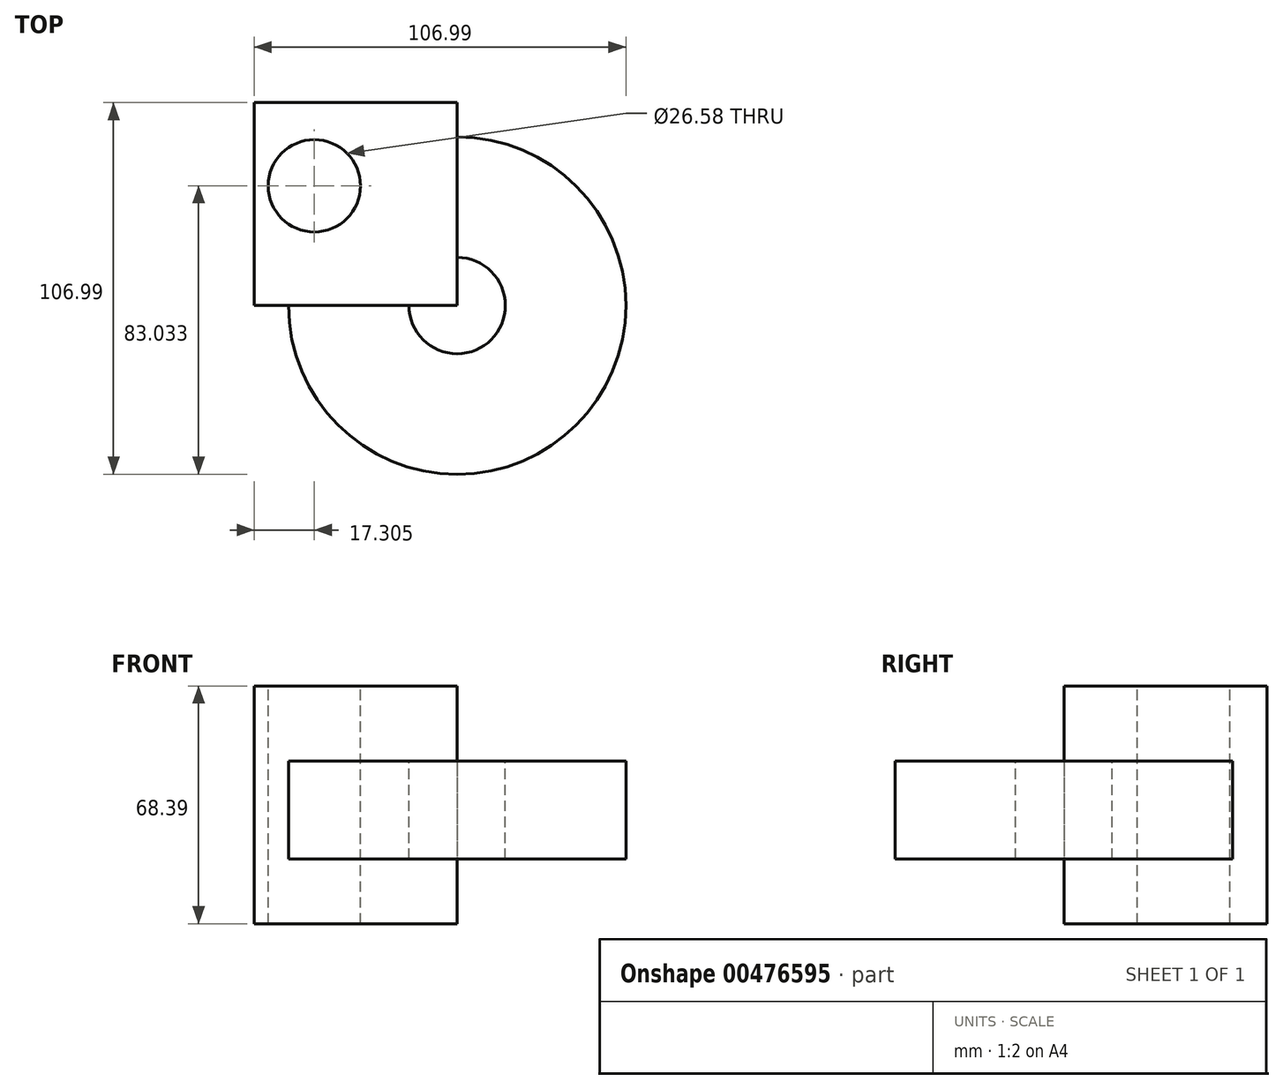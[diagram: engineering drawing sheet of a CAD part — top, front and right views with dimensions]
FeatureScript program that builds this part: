
annotation { "Feature Type Name" : "Feature", "Feature Type Description" : "" }
export const myFeature = defineFeature(function(context is Context, id is Id, definition is map)
    precondition{}
    {
        {
            var Q0;
            Q0=qCreatedBy(makeId("Top.planeOp"),FACE);
            var sketch = newSketch(context, id + "F0", { "sketchPlane" : qUnion([Q0])});
            skLineSegment(sketch, "E0.bottom", {"start": v(-41.3, -21.03) * mm, "end": v(17.13, -21.03) * mm});
            skLineSegment(sketch, "E0.top", {"start": v(-41.3, 37.4) * mm, "end": v(17.13, 37.4) * mm});
            skLineSegment(sketch, "E0.left", {"start": v(-41.3, -21.03) * mm, "end": v(-41.3, 37.4) * mm});
            skLineSegment(sketch, "E0.right", {"start": v(17.13, -21.03) * mm, "end": v(17.13, 37.4) * mm});
            skSolve(sketch);
        }
        {
            var Q0;
            Q0=makeQuery(id+"F0.imprint","IMPRINT",FACE,{"disambiguationData":[TD([[makeQuery(id+"F0.imprint","IMPRINT",EDGE,{"derivedFrom":sQuery(id+"F0.wireOp",EDGE,"E0.bottom")}),1.0]])]});
            extrude(context, id + "F1", {"entities" : qUnion([Q0]), "depth" : 68.4 * mm});
        }
        {
            var Q0;
            Q0=makeQuery(id+"F1.opExtrude","SWEPT_FACE",FACE,{"disambiguationData":[OSD([sQuery(id+"F0.wireOp",EDGE,"E0.bottom")])]});
            var sketch = newSketch(context, id + "F2", { "sketchPlane" : qUnion([Q0])});
            skLineSegment(sketch, "E1.bottom", {"start": v(-31.44, 46.76) * mm, "end": v(3.25, 46.76) * mm});
            skLineSegment(sketch, "E1.top", {"start": v(-31.44, 18.6) * mm, "end": v(3.25, 18.6) * mm});
            skLineSegment(sketch, "E1.left", {"start": v(-31.44, 46.76) * mm, "end": v(-31.44, 18.6) * mm});
            skLineSegment(sketch, "E1.right", {"start": v(3.25, 46.76) * mm, "end": v(3.25, 18.6) * mm});
            skSolve(sketch);
        }
        {
            var Q0;
            Q0 = qSketchRegion(id + "F2", true);
            var Q1;
            Q1=makeQuery(id+"F1.opExtrude","SWEPT_EDGE",EDGE,{"disambiguationData":[OSD([sQuery(id+"F0.wireOp",EDGE,"E0.bottom"),sQuery(id+"F0.wireOp",EDGE,"E0.right")])]});
            revolve(context, id + "F3", {"operationType" : NewBodyOperationType.ADD, "surfaceOperationType" : NewSurfaceOperationType.NEW, "entities" : qUnion([Q0]), "axis" : qUnion([Q1]), "revolveType" : RevolveType.FULL});
        }
        {
            var Q0;
            Q0=makeQuery(id+"F1.opExtrude","CAP_FACE",FACE,{"disambiguationData":[OSD([sQuery(id+"F0.wireOp",EDGE,"E0.bottom"),sQuery(id+"F0.wireOp",EDGE,"E0.top"),sQuery(id+"F0.wireOp",EDGE,"E0.left"),sQuery(id+"F0.wireOp",EDGE,"E0.right")])],"isStart":false});
            var sketch = newSketch(context, id + "F4", { "sketchPlane" : qUnion([Q0])});
            skCircle(sketch, "E2", {"center": v(-23.98, 13.43) * mm, "radius": 13.29 * mm});
            skSolve(sketch);
        }
        {
            var Q0;
            Q0 = qSketchRegion(id + "F4", true);
            extrude(context, id + "F5", {"entities" : qUnion([Q0]), "operationType" : NewBodyOperationType.REMOVE, "oppositeDirection" : true, "depth" : 140.97 * mm, "offsetDistance" : 25.4 * mm});
        }
    });
